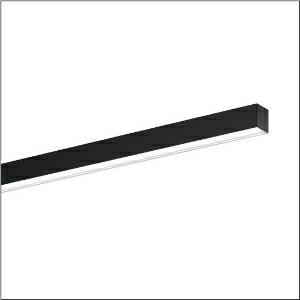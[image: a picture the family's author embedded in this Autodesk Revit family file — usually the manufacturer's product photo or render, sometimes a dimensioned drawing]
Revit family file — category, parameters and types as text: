
# Revit family: silica_r__21_51mx20da32bb_5abe
name_source: partatom
category: Lighting Fixtures
units: mm (PartAtom-declared; Revit-internal decimal feet)

## family parameters
Cut with Voids When Loaded = No
Host = Face
Light Source = No
Part Type = Normal
Room Calculation Point = No
Round Connector Dimension = Use Diameter
Shared = No

## types (1)
- --- (1 x LED, 2400 lm, 16.1 W, 3000K)
    Apparent Load = 16 VA
    CIE Flux Codes = 48 79 96 100 100
    Color Rendering = 80
    Color Temperature = 3000K
    Default Elevation = 1800 mm
    Description = Silica® 21, office luminaire, primary optical cover: cover, of PMMA, opal, light emission: direct distribution, primary light characteristic: symmetric, installation type: surface-mounted, LED, rated luminous flux: 2.400lm, luminous efficacy: 149lm/W, light colour: 830, colour temperature: 3000K, control gear: DALI 2, with terminal, 3+2-pole, max. 2.5mm², mains connection: 220..240V, AC, 50/60Hz, rated input power: 16.1W, luminaire housing, of aluminium, matt jet black (RAL 9005), length: 1.204mm, width: 53mm, height: 53mm, protection rating (complete): IP20, insulation class (complete): insulation class I (protective earthing), certification: CE, permissible operating ambient temperature: 0..+35°C, standard: EN 50419, packaging unit: 1 piece
    Height = 53 mm
    Lamp = 1 x LED
    Lamp Light Flux = 2400 lm
    Lamp Power = 16.1 W
    Lamp count = 1
    Length = 1204 mm
    Luminous efficacy = 149 lm/W
    Manufacturer = Siteco
    ModVariant = No
    Model = 51MX20DA32BB
    Mounting Place = Ceiling
    Mounting Type = Surface mounted
    Number of Poles = 1
    OnlyDefault = Yes
    Power Factor = 1
    Product Name = Silica® 21
    Product group = office luminaire | ceiling mounted
    ProductGroupID = 301
    Protection Class = Protection class I
    Protection Degree = IP 20
    RLX_Detail_Level = 1
    RLX_Emergency_Light_Flux = 0 lm
    RLX_Emergency_Type = 0
    RLX_Emergency_Type_DB = No
    RlxData = <blob elided: 25329 chars, md5=3c4c9f2b>
    Socket = socket
    Standby Power = 0 W
    System Light Flux = 2400 lm
    System Power = 16 W
    Type Comments = factory setting: luminous flux: 100 % | dim-lin: 254 | 233 mA
    Type Image = l_1335925.jpg
    URL = http://relux.com
    VarID = @adj_004265
    Voltage = 0 V
    Weight = 0.00 kg
    Width = 53 mm

## geometry (parser evidence)
native form markers: Blend x4, Sweep x9
no freeform markers — native parametric forms only
